# Revit family: Shower-Shower_Hose-KOHLER-K-11628BR_1
name_source: partatom
category: Plumbing Fixtures
revit_build: Autodesk Revit 2017 (Build: 20160225_1515(x64)
units: mm (PartAtom-declared; Revit-internal decimal feet)

## family parameters
Cut with Voids When Loaded = No
Host = Face
OmniClass Number = 23.31.17.00
OmniClass Title = Showers
Part Type = Normal
Room Calculation Point = No
Round Connector Dimension = Use Diameter
Shared = No

## types (4) — shared parameters
ADA Compliant = No
Assembly Code = D2010700
CW Connection = No
Cold Water Inlet = Cold Water Inlet
Date Modified = 09/01/2021
Default Elevation = 15"
Description = Smooth flexible for hand shower 1.50m
Drain Included = No
HW Connection = Yes
Height = 59 1/16"
Hot Water Inlet = Hot Water Inlet
Length = 59 1/16"
Manufacturer = KOHLER Co.
MasterFormat 1995 = 15410
MasterFormat 2004 = 22.41.23
Material = Premium Metal Construction
Pipe Finish = Kohler-Plastic-58-Thunder_Grey
Product Documentation Link = http://resources.kohler.com
Product Page URL = https://br.kohler.com
Tempered Water Supply1 = Tempered Water Supply1
Tempered Water Supply2 = Tempered Water Supply2
URL = https://br.kohler.com
Vent Connection = No
Waste Connection = No
Waste Water Outlet = Waste Water Outlet
WaterSense Certified = No
Width = 1/2"

## per-type parameters (varying)
| type | Finish | Model | Type |
| CP-Polished Chrome | Kohler-Metal-CP-Polished_Chrome | K-11628BR-CP | 1 |
| BN-Vibrant Brushed Nickel | Kohler-Metal-BN-Vibrant_Brushed_Nickel | K-11628BR-BN | 2 |
| BL-Matte Black | Kohler-Metal-BL-Matte_Black | K-11628BR-BL | 3 |
| RGD-Polished Rose Gold | Kohler-Metal-RGD-Polished_Rose_Gold | K-11628BR-RGD | 4 |

## geometry (parser evidence)
native form markers: Sweep x6
no freeform markers — native parametric forms only
